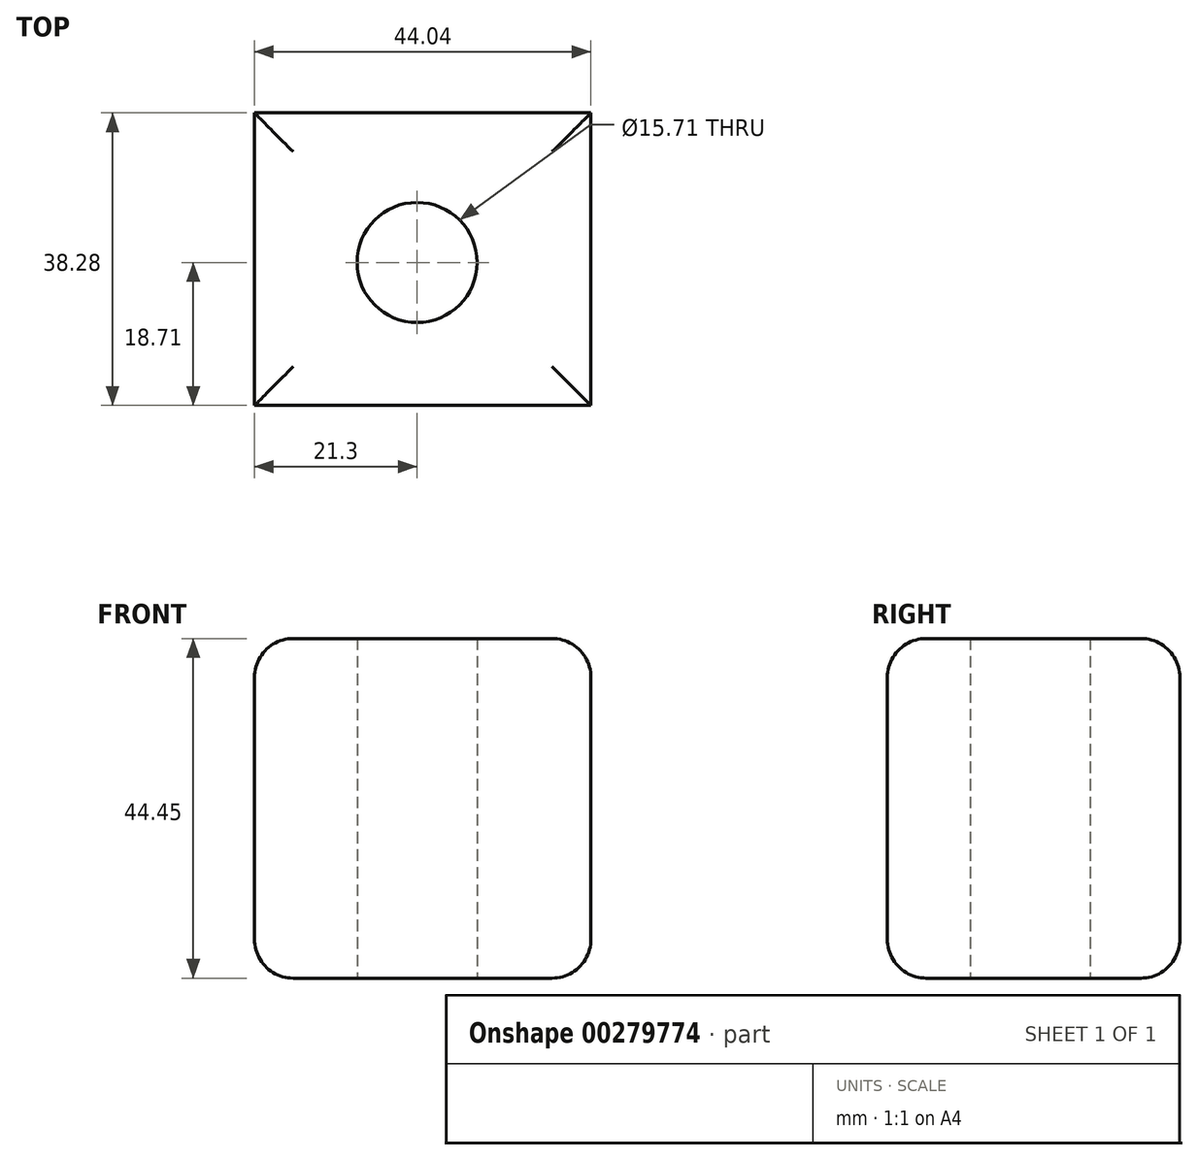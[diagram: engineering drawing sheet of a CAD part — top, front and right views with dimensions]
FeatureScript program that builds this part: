
annotation { "Feature Type Name" : "Feature", "Feature Type Description" : "" }
export const myFeature = defineFeature(function(context is Context, id is Id, definition is map)
    precondition{}
    {
        {
            var Q0;
            Q0=qCreatedBy(makeId("Top.planeOp"),FACE);
            var sketch = newSketch(context, id + "F0", { "sketchPlane" : qUnion([Q0])});
            skLineSegment(sketch, "E0.bottom", {"start": v(-21.3, -18.7) * mm, "end": v(22.74, -18.7) * mm});
            skLineSegment(sketch, "E0.top", {"start": v(-21.3, 19.57) * mm, "end": v(22.74, 19.57) * mm});
            skLineSegment(sketch, "E0.left", {"start": v(-21.3, -18.7) * mm, "end": v(-21.3, 19.57) * mm});
            skLineSegment(sketch, "E0.right", {"start": v(22.74, -18.7) * mm, "end": v(22.74, 19.57) * mm});
            skCircle(sketch, "E1", {"center": v(0, 0) * mm, "radius": 7.86 * mm});
            skSolve(sketch);
        }
        {
            var Q0;
            Q0=makeQuery(id+"F0.imprint","IMPRINT",FACE,{"disambiguationData":[TD([[makeQuery(id+"F0.imprint","IMPRINT",EDGE,{"derivedFrom":sQuery(id+"F0.wireOp",EDGE,"E0.bottom")}),1.0]])]});
            extrude(context, id + "F1", {"entities" : qUnion([Q0]), "depth" : 44.45 * mm});
        }
        {
            var Q0;
            Q0=makeQuery(id+"F1.opExtrude","CAP_EDGE",EDGE,{"disambiguationData":[OSD([sQuery(id+"F0.wireOp",EDGE,"E0.bottom")])],"isStart":false});
            var Q1;
            Q1=makeQuery(id+"F1.opExtrude","CAP_EDGE",EDGE,{"disambiguationData":[OSD([sQuery(id+"F0.wireOp",EDGE,"E0.right")])],"isStart":false});
            var Q2;
            Q2=makeQuery(id+"F1.opExtrude","CAP_EDGE",EDGE,{"disambiguationData":[OSD([sQuery(id+"F0.wireOp",EDGE,"E0.top")])],"isStart":false});
            var Q3;
            Q3=makeQuery(id+"F1.opExtrude","CAP_EDGE",EDGE,{"disambiguationData":[OSD([sQuery(id+"F0.wireOp",EDGE,"E0.left")])],"isStart":false});
            fillet(context, id + "F2", {"entities" : qUnion([Q0, Q1, Q2, Q3]), "radius" : 5.08 * mm, "tangentPropagation" : true, "allowEdgeOverflow" : false});
        }
        {
            var Q0;
            Q0=makeQuery(id+"F1.opExtrude","CAP_EDGE",EDGE,{"disambiguationData":[OSD([sQuery(id+"F0.wireOp",EDGE,"E0.top")])],"isStart":true});
            var Q1;
            Q1=makeQuery(id+"F1.opExtrude","CAP_EDGE",EDGE,{"disambiguationData":[OSD([sQuery(id+"F0.wireOp",EDGE,"E0.left")])],"isStart":true});
            var Q2;
            Q2=makeQuery(id+"F1.opExtrude","CAP_EDGE",EDGE,{"disambiguationData":[OSD([sQuery(id+"F0.wireOp",EDGE,"E0.bottom")])],"isStart":true});
            var Q3;
            Q3=makeQuery(id+"F1.opExtrude","CAP_EDGE",EDGE,{"disambiguationData":[OSD([sQuery(id+"F0.wireOp",EDGE,"E0.right")])],"isStart":true});
            fillet(context, id + "F3", {"entities" : qUnion([Q0, Q1, Q2, Q3]), "radius" : 5.08 * mm, "tangentPropagation" : true, "allowEdgeOverflow" : false});
        }
    });
